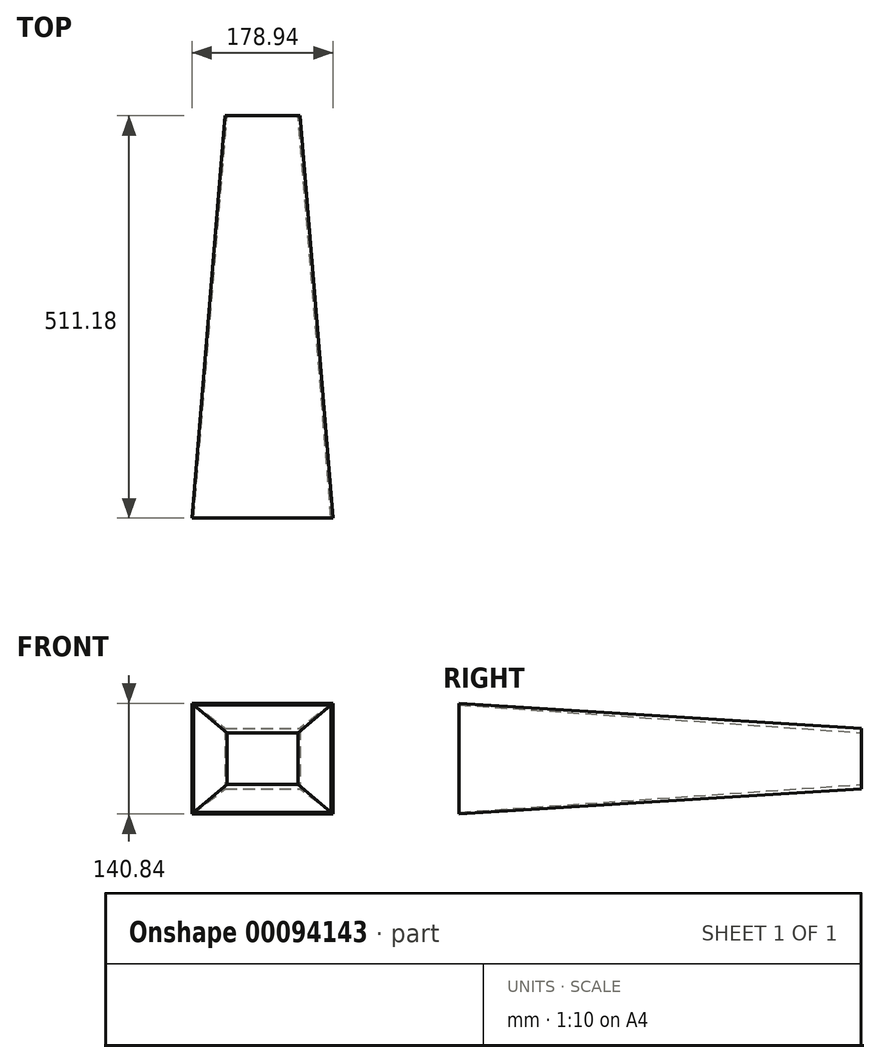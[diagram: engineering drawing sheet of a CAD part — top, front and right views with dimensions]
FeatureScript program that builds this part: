
annotation { "Feature Type Name" : "Feature", "Feature Type Description" : "" }
export const myFeature = defineFeature(function(context is Context, id is Id, definition is map)
    precondition{}
    {
        {
            var Q0;
            Q0=qCreatedBy(makeId("Front.planeOp"),FACE);
            var sketch = newSketch(context, id + "F0", { "sketchPlane" : qUnion([Q0])});
            skLineSegment(sketch, "E0.bottom", {"start": v(44.96, 32.9) * mm, "end": v(-44.96, 32.9) * mm});
            skLineSegment(sketch, "E0.top", {"start": v(44.96, -32.9) * mm, "end": v(-44.96, -32.9) * mm});
            skLineSegment(sketch, "E0.left", {"start": v(44.96, 32.9) * mm, "end": v(44.96, -32.9) * mm});
            skLineSegment(sketch, "E0.right", {"start": v(-44.96, 32.9) * mm, "end": v(-44.96, -32.9) * mm});
            skPoint(sketch, "E0.middle", {"position": v(0, 0) * mm});
            skSolve(sketch);
        }
        {
            var Q0;
            Q0=qCreatedBy(makeId("Front.planeOp"),FACE);
            cPlane(context, id + "F1", {"entities" : qUnion([Q0]), "cplaneType" : CPlaneType.OFFSET, "offset" : 511.17 * mm, "width" : 152.4 * mm, "height" : 152.4 * mm});
        }
        {
            var Q0;
            Q0=qCreatedBy(id+"F1.planeOp",FACE);
            var sketch = newSketch(context, id + "F2", { "sketchPlane" : qUnion([Q0])});
            skLineSegment(sketch, "E1.bottom", {"start": v(87.31, 68.26) * mm, "end": v(-87.31, 68.26) * mm});
            skLineSegment(sketch, "E1.top", {"start": v(87.31, -68.26) * mm, "end": v(-87.31, -68.26) * mm});
            skLineSegment(sketch, "E1.left", {"start": v(87.31, 68.26) * mm, "end": v(87.31, -68.26) * mm});
            skLineSegment(sketch, "E1.right", {"start": v(-87.31, 68.26) * mm, "end": v(-87.31, -68.26) * mm});
            skPoint(sketch, "E1.middle", {"position": v(0, 0) * mm});
            skSolve(sketch);
        }
        {
            var Q0;
            Q0=makeQuery(id+"F0.imprint","IMPRINT",FACE,{"disambiguationData":[TD([[makeQuery(id+"F0.imprint","IMPRINT",EDGE,{"derivedFrom":sQuery(id+"F0.wireOp",EDGE,"E0.bottom")}),1.0]])]});
            var Q1;
            Q1=makeQuery(id+"F2.imprint","IMPRINT",FACE,{"disambiguationData":[TD([[makeQuery(id+"F2.imprint","IMPRINT",EDGE,{"derivedFrom":sQuery(id+"F2.wireOp",EDGE,"E1.bottom")}),1.0]])]});
            loft(context, id + "F3", {"sheetProfilesArray" : [{ "sheetProfileEntities" : qUnion([Q0]) }, { "sheetProfileEntities" : qUnion([Q1]) }]});
        }
        {
            var Q0;
            Q0=qCreatedBy(makeId("Front.planeOp"),FACE);
            var sketch = newSketch(context, id + "F4", { "sketchPlane" : qUnion([Q0])});
            skLineSegment(sketch, "E2.bottom", {"start": v(-47.62, 38.6) * mm, "end": v(47.63, 38.6) * mm});
            skLineSegment(sketch, "E2.top", {"start": v(-47.63, -38.6) * mm, "end": v(47.62, -38.6) * mm});
            skLineSegment(sketch, "E2.left", {"start": v(-47.62, 38.6) * mm, "end": v(-47.63, -38.6) * mm});
            skLineSegment(sketch, "E2.right", {"start": v(47.63, 38.6) * mm, "end": v(47.62, -38.6) * mm});
            skPoint(sketch, "E2.middle", {"position": v(0, 0) * mm});
            skSolve(sketch);
        }
        {
            var Q0;
            Q0=qCreatedBy(id+"F1.planeOp",FACE);
            var sketch = newSketch(context, id + "F5", { "sketchPlane" : qUnion([Q0])});
            skLineSegment(sketch, "E3.bottom", {"start": v(89.47, 70.42) * mm, "end": v(-89.47, 70.42) * mm});
            skLineSegment(sketch, "E3.top", {"start": v(89.47, -70.42) * mm, "end": v(-89.47, -70.42) * mm});
            skLineSegment(sketch, "E3.left", {"start": v(89.47, 70.42) * mm, "end": v(89.47, -70.42) * mm});
            skLineSegment(sketch, "E3.right", {"start": v(-89.47, 70.42) * mm, "end": v(-89.47, -70.42) * mm});
            skPoint(sketch, "E3.middle", {"position": v(0, 0) * mm});
            skSolve(sketch);
        }
        {
            var Q1;
            Q1 = qSketchRegion(id + "F5", true);
            var Q2;
            Q2 = qSketchRegion(id + "F4", true);
            loft(context, id + "F6", {"operationType" : NewBodyOperationType.ADD, "sheetProfilesArray" : [{ "sheetProfileEntities" : qUnion([Q1]) }, { "sheetProfileEntities" : qUnion([Q2]) }]});
        }
        {
            var Q1;
            Q1 = qSketchRegion(id + "F2", true);
            var Q2;
            Q2 = qSketchRegion(id + "F0", true);
            loft(context, id + "F7", {"operationType" : NewBodyOperationType.REMOVE, "sheetProfilesArray" : [{ "sheetProfileEntities" : qUnion([Q1]) }, { "sheetProfileEntities" : qUnion([Q2]) }]});
        }
    });
